# Revit family: Wrestling_Mat_Storage-PSS-4090
name_source: partatom
category: Specialty Equipment
revit_build: Autodesk Revit 2018 (Build: 20170907_2315(x64)
units: mm (PartAtom-declared; Revit-internal decimal feet)

## family parameters
Always vertical = Yes
Cut with Voids When Loaded = No
OmniClass Number = 23.40.50.34.34
OmniClass Title = Equipment Storage Racks
Part Type = Normal
Room Calculation Point = No
Round Connector Dimension = Use Diameter
Shared = No
Work Plane-Based = No

## types (2) — shared parameters
Assembly Code = E1020900
CSI MasterFormat = 11 66 23
Description = Wrestling Mat Storage System
Length = 40' - 0"
Manufacturer = Performance Sports Systems
Mat Color = Generic - Wrestling Mat
Product Page URL = http://www.perfsports.com
Sling Material = Vinyl Coated Fabric - Performance Sports Systems - C04 Royal Blue
Superstructure Finish = Powder Coat - Performance Sports Systems - Black
URL = http://www.perfsports.com

## per-type parameters (varying)
| type | BIM Version | Model | Show Lower Sling |
| 4090 - Single Sling | v3.1 | 4090 | No |
| 4090DS - Double Sling Vertical | v1.1 | 4090DS | Yes |

## geometry (parser evidence)
native form markers: Blend x70, Sweep x10
no freeform markers — native parametric forms only
